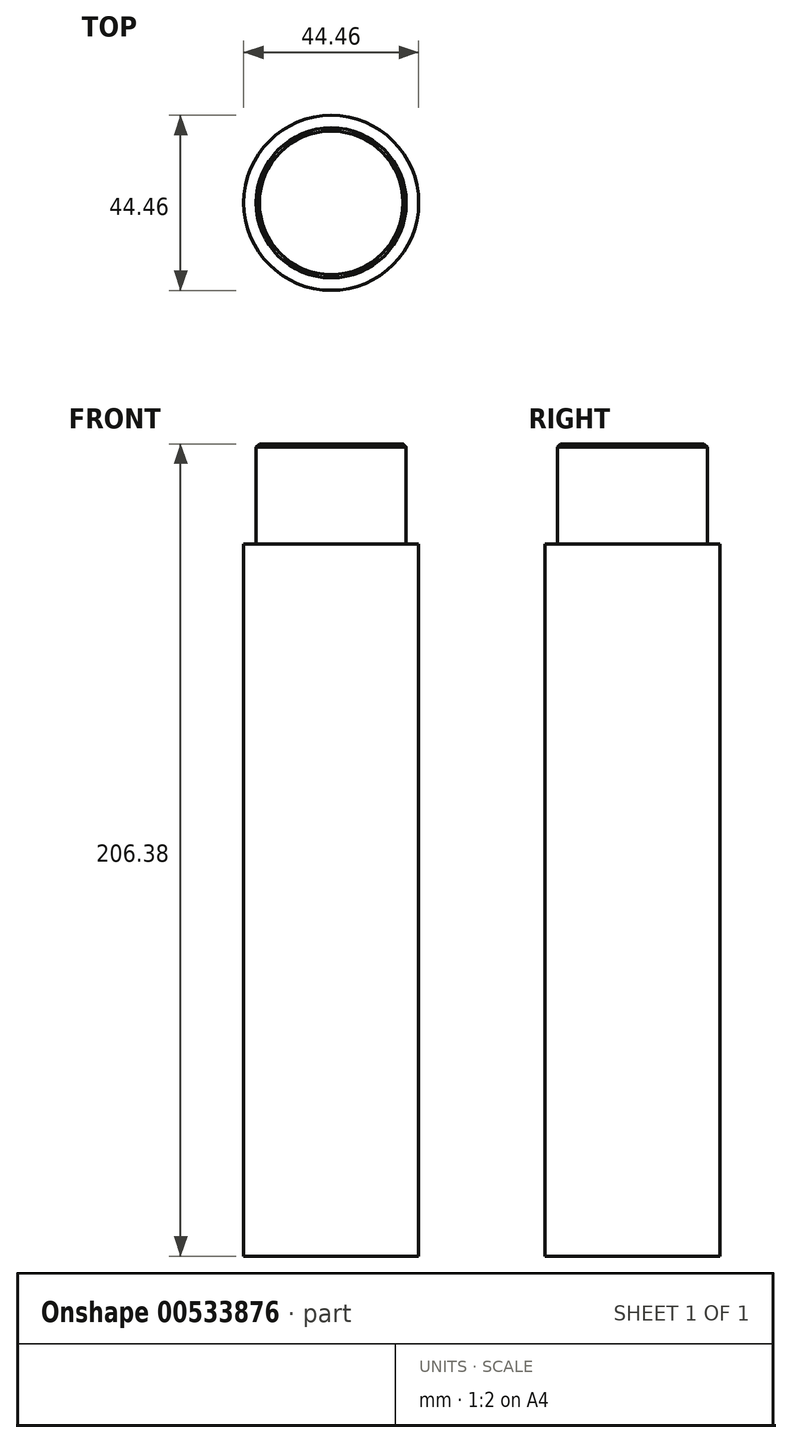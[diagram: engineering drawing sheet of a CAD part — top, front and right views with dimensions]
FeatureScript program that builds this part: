
annotation { "Feature Type Name" : "Feature", "Feature Type Description" : "" }
export const myFeature = defineFeature(function(context is Context, id is Id, definition is map)
    precondition{}
    {
        {
            var Q0;
            Q0=qCreatedBy(makeId("Top.planeOp"),FACE);
            var sketch = newSketch(context, id + "F0", { "sketchPlane" : qUnion([Q0])});
            skCircle(sketch, "E0.0", {"center": v(0, 0) * mm, "radius": 22.23 * mm});
            skSolve(sketch);
        }
        {
            var Q0;
            Q0 = qSketchRegion(id + "F0", true);
            extrude(context, id + "F1", {"entities" : qUnion([Q0]), "depth" : 180.97 * mm, "offsetDistance" : 25.4 * mm});
        }
        {
            var Q0;
            Q0=makeQuery(id+"F1.opExtrude","CAP_FACE",FACE,{"disambiguationData":[OSD([sQuery(id+"F0.wireOp",EDGE,"E0.0")])],"isStart":false});
            var sketch = newSketch(context, id + "F2", { "sketchPlane" : qUnion([Q0])});
            skCircle(sketch, "E1", {"center": v(0, 0) * mm, "radius": 19.05 * mm});
            skSolve(sketch);
        }
        {
            var Q0;
            Q0 = qSketchRegion(id + "F2", true);
            extrude(context, id + "F3", {"entities" : qUnion([Q0]), "operationType" : NewBodyOperationType.ADD, "depth" : 25.4 * mm, "offsetDistance" : 25.4 * mm});
        }
        {
            var Q0;
            Q0=makeQuery(id+"F3.opExtrude","CAP_EDGE",EDGE,{"disambiguationData":[OSD([sQuery(id+"F2.wireOp",EDGE,"E1")])],"isStart":false});
            chamfer(context, id + "F4", {"entities" : qUnion([Q0]), "width" : 0.8 * mm, "tangentPropagation" : true});
        }
    });
